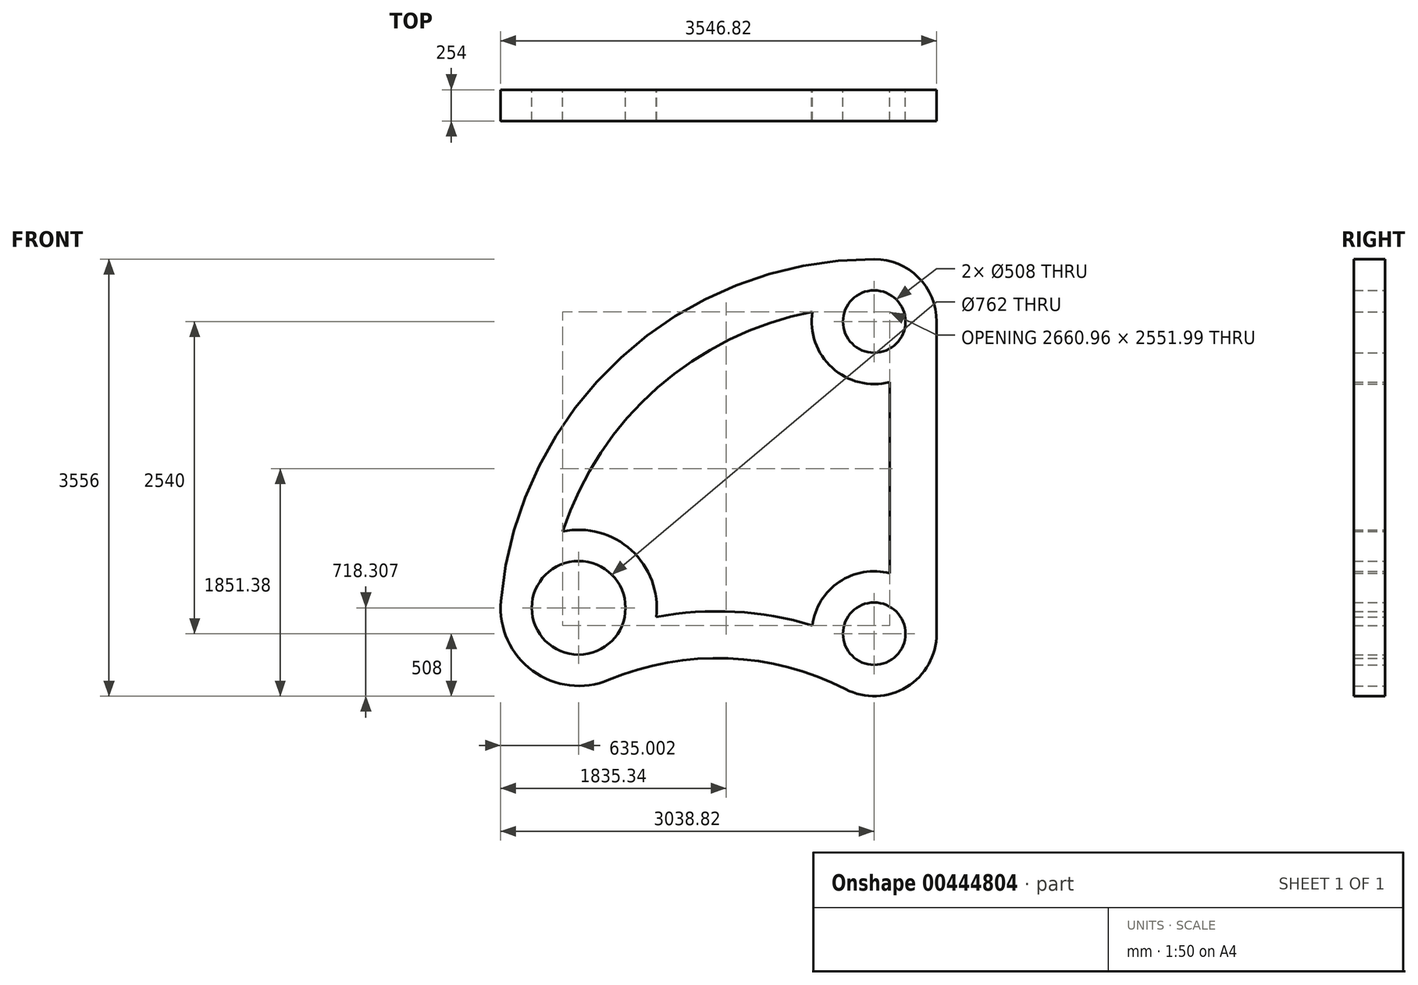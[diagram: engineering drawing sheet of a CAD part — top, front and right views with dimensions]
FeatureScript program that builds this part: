
annotation { "Feature Type Name" : "Feature", "Feature Type Description" : "" }
export const myFeature = defineFeature(function(context is Context, id is Id, definition is map)
    precondition{}
    {
        {
            var Q0;
            Q0=qCreatedBy(makeId("Front.planeOp"),FACE);
            var sketch = newSketch(context, id + "F0", { "sketchPlane" : qUnion([Q0])});
            skCircle(sketch, "E0", {"center": v(0, 0) * mm, "radius": 254 * mm});
            skArc(sketch, "E1", {"start": v(-232.28, -451.79) * mm, "mid": v(264.64, -433.63) * mm, "end": v(508, 0) * mm});
            skCircle(sketch, "E2", {"center": v(0, 2540) * mm, "radius": 254 * mm});
            skArc(sketch, "E3", {"start": v(508, 2540) * mm, "mid": v(359.21, 2899.21) * mm, "end": v(0, 3048) * mm});
            skLineSegment(sketch, "E4", {"start": v(508, 0) * mm, "end": v(508, 2540) * mm});
            skCircle(sketch, "E5", {"center": v(-2403.82, 210.3) * mm, "radius": 381 * mm});
            skArc(sketch, "E6", {"start": v(-3036.4, 265.65) * mm, "mid": v(-2778.5, -302.37) * mm, "end": v(-2158.97, -375.6) * mm});
            skArc(sketch, "E7.trimOffspring", {"start": v(-232.28, -451.79) * mm, "mid": v(-1187.2, -200.6) * mm, "end": v(-2158.97, -375.6) * mm});
            skArc(sketch, "E8.trimOffspring", {"start": v(-503.51, 67.39) * mm, "mid": v(-1134.23, 178.32) * mm, "end": v(-1773.21, 135.7) * mm});
            skArc(sketch, "E9.trimOffspring", {"start": v(-1773.21, 135.7) * mm, "mid": v(-1975.14, 678.78) * mm, "end": v(-2533.96, 831.83) * mm});
            skArc(sketch, "E10.trimOffspring", {"start": v(127, 491.87) * mm, "mid": v(-283.7, 421.4) * mm, "end": v(-503.51, 67.39) * mm});
            skLineSegment(sketch, "E11.trimOffspring", {"start": v(127, 491.87) * mm, "end": v(127, 2048.13) * mm});
            skArc(sketch, "E12.trimOffspring", {"start": v(-501.76, 2619.38) * mm, "mid": v(-1761.46, 2002.54) * mm, "end": v(-2533.96, 831.83) * mm});
            skArc(sketch, "E13.trimOffspring", {"start": v(-501.76, 2619.38) * mm, "mid": v(-341.6, 2164) * mm, "end": v(127, 2048.13) * mm});
            skArc(sketch, "E14.trimOffspring", {"start": v(0, 3048) * mm, "mid": v(-2059.2, 2247.22) * mm, "end": v(-3036.4, 265.65) * mm});
            skSolve(sketch);
        }
        {
            var Q0;
            Q0=makeQuery(id+"F0.imprint","IMPRINT",FACE,{"disambiguationData":[TD([[makeQuery(id+"F0.imprint","IMPRINT",EDGE,{"derivedFrom":sQuery(id+"F0.wireOp",EDGE,"E0")}),-1.0]])]});
            extrude(context, id + "F1", {"entities" : qUnion([Q0]), "depth" : 254 * mm});
        }
    });
